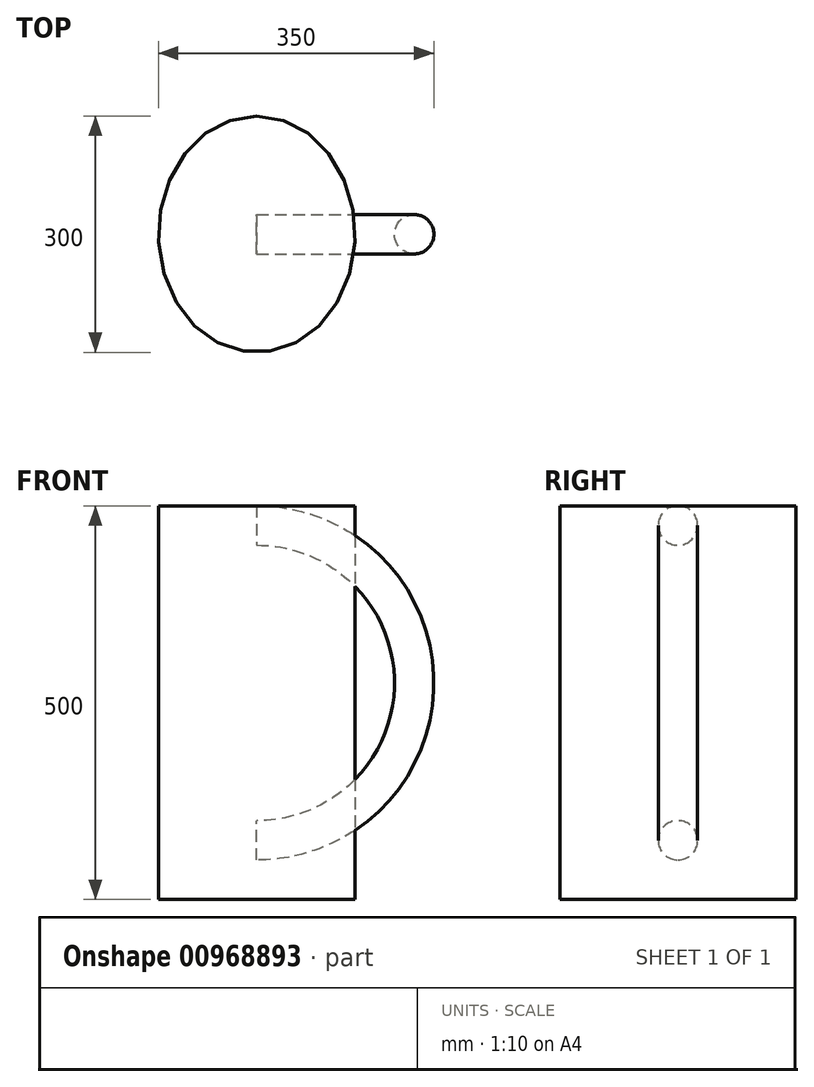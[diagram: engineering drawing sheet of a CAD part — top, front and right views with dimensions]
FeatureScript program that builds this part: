
annotation { "Feature Type Name" : "Feature", "Feature Type Description" : "" }
export const myFeature = defineFeature(function(context is Context, id is Id, definition is map)
    precondition{}
    {
        {
            var Q0;
            Q0=qCreatedBy(makeId("Top.planeOp"),FACE);
            var sketch = newSketch(context, id + "F0", { "sketchPlane" : qUnion([Q0])});
            skLineSegment(sketch, "E0", {"start": v(-165.81, 0) * mm, "end": v(189.2, 0) * mm});
            skEllipse(sketch, "E1", {"center": v(0, 0) * mm, "majorRadius": 150 * mm, "minorRadius": 125 * mm, "majorAxis": v(0, 1)});
            skSolve(sketch);
        }
        {
            var Q0;
            Q0 = qSketchRegion(id + "F0", true);
            extrude(context, id + "F1", {"entities" : qUnion([Q0]), "depth" : 500 * mm, "offsetDistance" : 25 * mm});
        }
        {
            var Q0;
            Q0=qCreatedBy(makeId("Right.planeOp"),FACE);
            var sketch = newSketch(context, id + "F2", { "sketchPlane" : qUnion([Q0])});
            skLineSegment(sketch, "E2", {"start": v(0, 0) * mm, "end": v(0, 500) * mm});
            skLineSegment(sketch, "E3", {"start": v(0, 0) * mm, "end": v(0, 75) * mm});
            skCircle(sketch, "E4", {"center": v(0, 75) * mm, "radius": 25 * mm});
            skLineSegment(sketch, "E5", {"start": v(0, 75) * mm, "end": v(0, 275) * mm});
            skLineSegment(sketch, "E6", {"start": v(0, 275) * mm, "end": v(-80.37, 275) * mm});
            skSolve(sketch);
        }
        {
            var Q0;
            Q0 = qSketchRegion(id + "F2", true);
            var Q1;
            Q1=sQuery(id+"F2.wireOp",EDGE,"E6");
            revolve(context, id + "F3", {"surfaceOperationType" : NewSurfaceOperationType.NEW, "entities" : qUnion([Q0]), "axis" : qUnion([Q1]), "revolveType" : RevolveType.ONE_DIRECTION, "angle" : 180 * degree});
        }
    });
